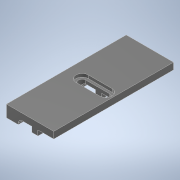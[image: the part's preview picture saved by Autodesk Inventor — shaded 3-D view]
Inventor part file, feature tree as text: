
AUTODESK INVENTOR PART (.ipt)
format: ipt  version: 2022 (Build 260153000, 153)  size: 181,760 bytes
history: native  units: in
note: dims shown in document units (in); Inventor stores cm internally (conversion verified against a paired STEP export)
features: extrude x6, sketch x6, fillet x1
ambient origin geometry x8: Origin, YZ Plane, XZ Plane, XY Plane, X Axis, Y Axis, Z Axis, Center Point
bodies: Solid1 (feature_tree)
feature tree (13):
  extrude  "Extrusion1"  Depth=1.9in
  extrude  "Extrusion2"  Depth=0.1875in
  extrude  "Extrusion3"  TaperAngle=0.0deg  [1 undecoded]
  fillet  "Fillet1"  Radius=1.5591in
  extrude  "Extrusion6"  Depth=0.0866in
  extrude  "Extrusion4"  Depth=0.0625in TaperAngle=0.0deg
  extrude  "Extrusion7"  Depth=0.06in
  sketch  "Sketch1"  dims[d0=0.75in d1=1.9in]
  sketch  "Sketch2"  dims[d2=0.1875in d3=0.0in d4=0.5625in]
  sketch  "Sketch3"  dims[d6=0.0625in d7=0.0in d8=0.0in d9=1.5591in]
  sketch  "Sketch4"  dims[d10=0.125in d11=0.0866in]
  sketch  "Sketch6"  dims[d12=0.0866in d13=0.0625in d14=0.0in]
  sketch  "Sketch7"  dims[d15=0.0312in d16=0.06in d17=0.375in d19=0.0in d20=0.0in d21=0.0827in d25=0.25in d26=0.1in d27=1.0in d28=0.0in d30=0.125in d31=0.2in d32=0.0in d33=0.0in d34=0.05in d35=0.0in]
note: 1 required parameter value undecoded (feature->parameter linkage not recoverable at this tier; creation-order binding heuristic only, values carry confidence <= 0.55)
